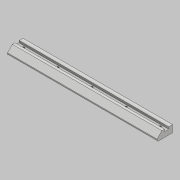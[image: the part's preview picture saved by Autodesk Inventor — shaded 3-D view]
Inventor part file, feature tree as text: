
AUTODESK INVENTOR PART (.ipt)
format: ipt  version: 2018 (Build 220112000, 112)  size: 111,616 bytes
history: native  units: mm
features: other x2, sketch x2, extrude x1, fillet x1, hole x1
ambient origin geometry x8: Origin, YZ Plane, XZ Plane, XY Plane, X Axis, Y Axis, Z Axis, Center Point
bodies: Body1 (feature_tree)
feature tree (7):
  other  "實體1"
  extrude  "擠出1"  Depth=28.0mm
  fillet  "圓角1"  Radius=15.0mm
  hole  "孔1"  [1 undecoded]
  other  "刪除面1"
  sketch  "草圖1"
  sketch  "草圖2"
note: 1 required parameter value undecoded (feature->parameter linkage not recoverable at this tier; creation-order binding heuristic only, values carry confidence <= 0.55)
